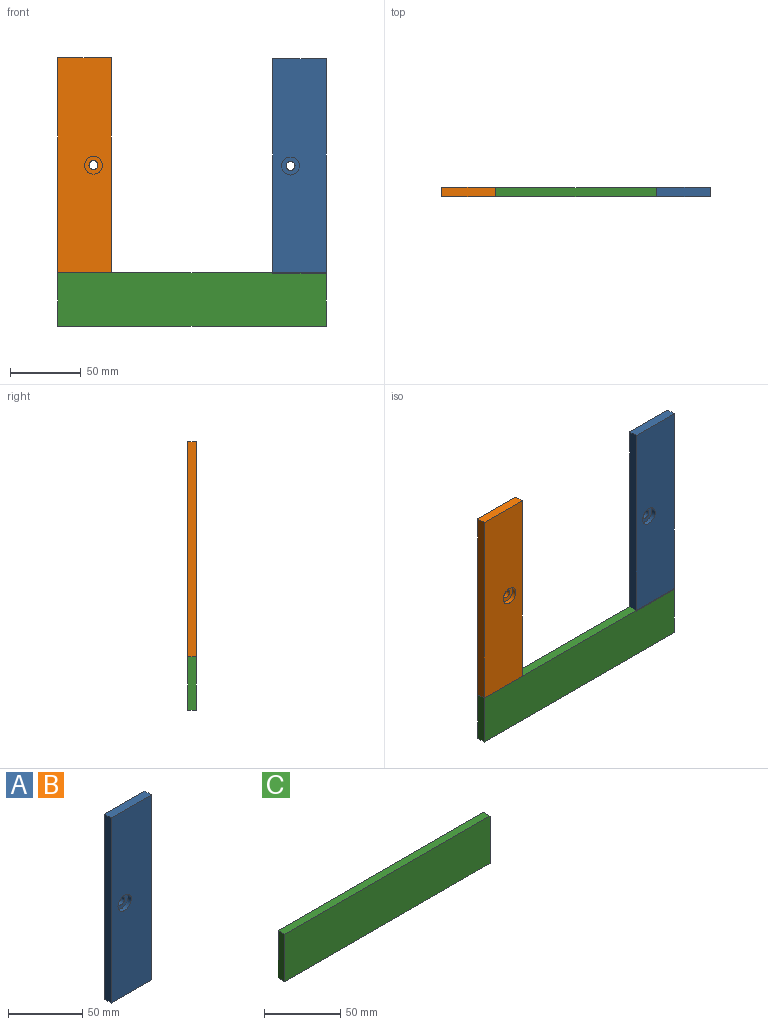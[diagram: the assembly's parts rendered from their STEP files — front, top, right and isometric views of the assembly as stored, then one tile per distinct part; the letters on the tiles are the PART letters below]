
ASSEMBLY  parts=3 mates=1
PART A: 9 faces, bbox 38.1x6.4x152.4 mm
  f0: plane 152.4x6.35mm, normal (-1,0,0), area 967.7mm2, adj f1,f3,f4,f5
  f1: plane 38.1x6.35mm, normal (0,0,-1), area 241.9mm2, adj f0,f2,f4,f5
  f2: plane 152.4x6.35mm, normal (1,0,0), area 967.7mm2, adj f1,f3,f4,f5
  f3: plane 38.1x6.35mm, normal (0,0,1), area 241.9mm2, adj f0,f2,f4,f5
  f4: plane 152.4x38.1mm, normal (0,-1,0), area 5679.8mm2, adj f0,f1,f2,f3,f6
  f5: plane 152.4x38.1mm, normal (0,1,0), area 5774.8mm2, adj f0,f1,f2,f3,f8
  f6: cylinder r=6.35mm len=12.7mm, axis (0,-1,0), area 126.7mm2, adj f4,f7
  f7: plane 12.7x12.7mm, normal (0,-1,0), area 95mm2, adj f6,f8
  f8: cylinder r=3.17mm len=6.35mm, axis (0,-1,0), area 63.3mm2, adj f5,f7
PART B: same geometry as A
PART C: 6 faces, bbox 190.5x6.4x38.1 mm
  f0: plane 38.1x6.35mm, normal (-1,0,0), area 241.9mm2, adj f1,f3,f4,f5
  f1: plane 190.5x6.35mm, normal (0,0,-1), area 1209.7mm2, adj f0,f2,f4,f5
  f2: plane 38.1x6.35mm, normal (1,0,0), area 241.9mm2, adj f1,f3,f4,f5
  f3: plane 190.5x6.35mm, normal (0,0,1), area 1209.7mm2, adj f0,f2,f4,f5
  f4: plane 190.5x38.1mm, normal (0,-1,0), area 7258.1mm2, adj f0,f1,f2,f3
  f5: plane 190.5x38.1mm, normal (0,1,0), area 7258.1mm2, adj f0,f1,f2,f3
PLACE A t=(60.33,21.2,-33.52)mm
PLACE B rot(axis=(0,-1,0),180deg) t=(-53.97,21.2,119.54)mm
PLACE C t=(-92.07,21.2,-70.96)mm
MATE planar C.f3 <-> B.f3  axis (0,0,1) through (-92.07,21.2,-32.86)mm
